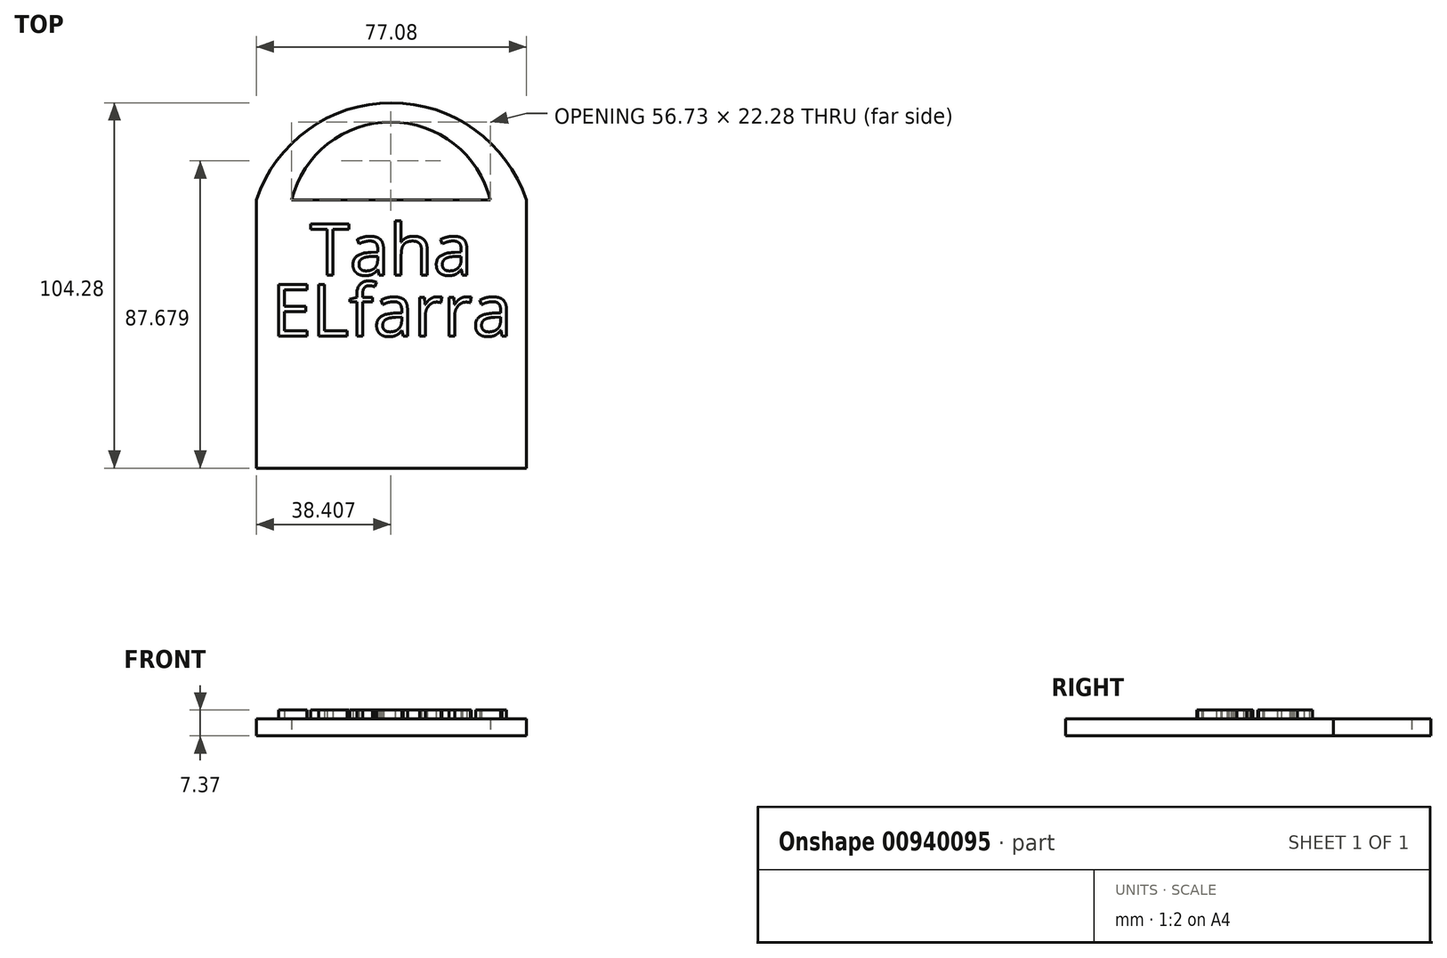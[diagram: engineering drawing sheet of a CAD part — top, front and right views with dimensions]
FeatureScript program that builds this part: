
annotation { "Feature Type Name" : "Feature", "Feature Type Description" : "" }
export const myFeature = defineFeature(function(context is Context, id is Id, definition is map)
    precondition{}
    {
        {
            var Q0;
            Q0=qCreatedBy(makeId("Top.planeOp"),FACE);
            var sketch = newSketch(context, id + "F0", { "sketchPlane" : qUnion([Q0])});
            skLineSegment(sketch, "E0.bottom", {"start": v(0, 0) * mm, "end": v(-77.08, 0) * mm});
            skLineSegment(sketch, "E0.top", {"start": v(0, -76.54) * mm, "end": v(-77.08, -76.54) * mm});
            skLineSegment(sketch, "E0.left", {"start": v(0, 0) * mm, "end": v(0, -76.54) * mm});
            skLineSegment(sketch, "E0.right", {"start": v(-77.08, 0) * mm, "end": v(-77.08, -76.54) * mm});
            skArc(sketch, "E1", {"start": v(0, 0) * mm, "mid": v(-38.54, 27.74) * mm, "end": v(-77.08, 0) * mm});
            skArc(sketch, "E2", {"start": v(-10.3, 0) * mm, "mid": v(-38.67, 22.28) * mm, "end": v(-67.04, 0) * mm});
            skSolve(sketch);
        }
        {
            var Q0;
            {var subQ0=sQuery(id+"F0.wireOp",EDGE,"E1");Q0=makeQuery(id+"F0.imprint","IMPRINT",FACE,{"disambiguationData":[TD([[makeQuery(id+"F0.imprint","IMPRINT",EDGE,{"derivedFrom":subQ0}),1.0]])]});}
            var Q1;
            Q1=makeQuery(id+"F0.imprint","IMPRINT",FACE,{"disambiguationData":[TD([[makeQuery(id+"F0.imprint","IMPRINT",EDGE,{"derivedFrom":sQuery(id+"F0.wireOp",EDGE,"E0.top")}),-1.0]])]});
            extrude(context, id + "F1", {"entities" : qUnion([Q0, Q1]), "depth" : 4.83 * mm, "offsetDistance" : 25.4 * mm});
        }
        {
            var Q0;
            Q0=makeQuery(id+"F1.opExtrude","CAP_FACE",FACE,{"disambiguationData":[OSD([sQuery(id+"F0.wireOp",EDGE,"E0.bottom"),sQuery(id+"F0.wireOp",EDGE,"E0.top"),sQuery(id+"F0.wireOp",EDGE,"E0.left"),sQuery(id+"F0.wireOp",EDGE,"E0.right"),sQuery(id+"F0.wireOp",EDGE,"E1"),sQuery(id+"F0.wireOp",EDGE,"E2")])],"isStart":false});
            var sketch = newSketch(context, id + "F2", { "sketchPlane" : qUnion([Q0])});
            skText(sketch, "E3", { "text": "Taha", "fontName": "OpenSans-Regular.ttf"});
            skText(sketch, "E4", { "text": "ELfarra", "fontName": "OpenSans-Regular.ttf"});
            const initialGuessF2  = {"E3": [-0.06172, -0.02141, 1, 0, 0.01465], "E4": [-0.0728, -0.03882, 1, 0, 0.01481]};
            skSetInitialGuess(sketch, initialGuessF2);
            skSolve(sketch);
        }
        {
            var Q0;
            Q0 = qSketchRegion(id + "F2", true);
            extrude(context, id + "F3", {"entities" : qUnion([Q0]), "operationType" : NewBodyOperationType.ADD, "depth" : 2.54 * mm, "offsetDistance" : 25.4 * mm});
        }
    });
